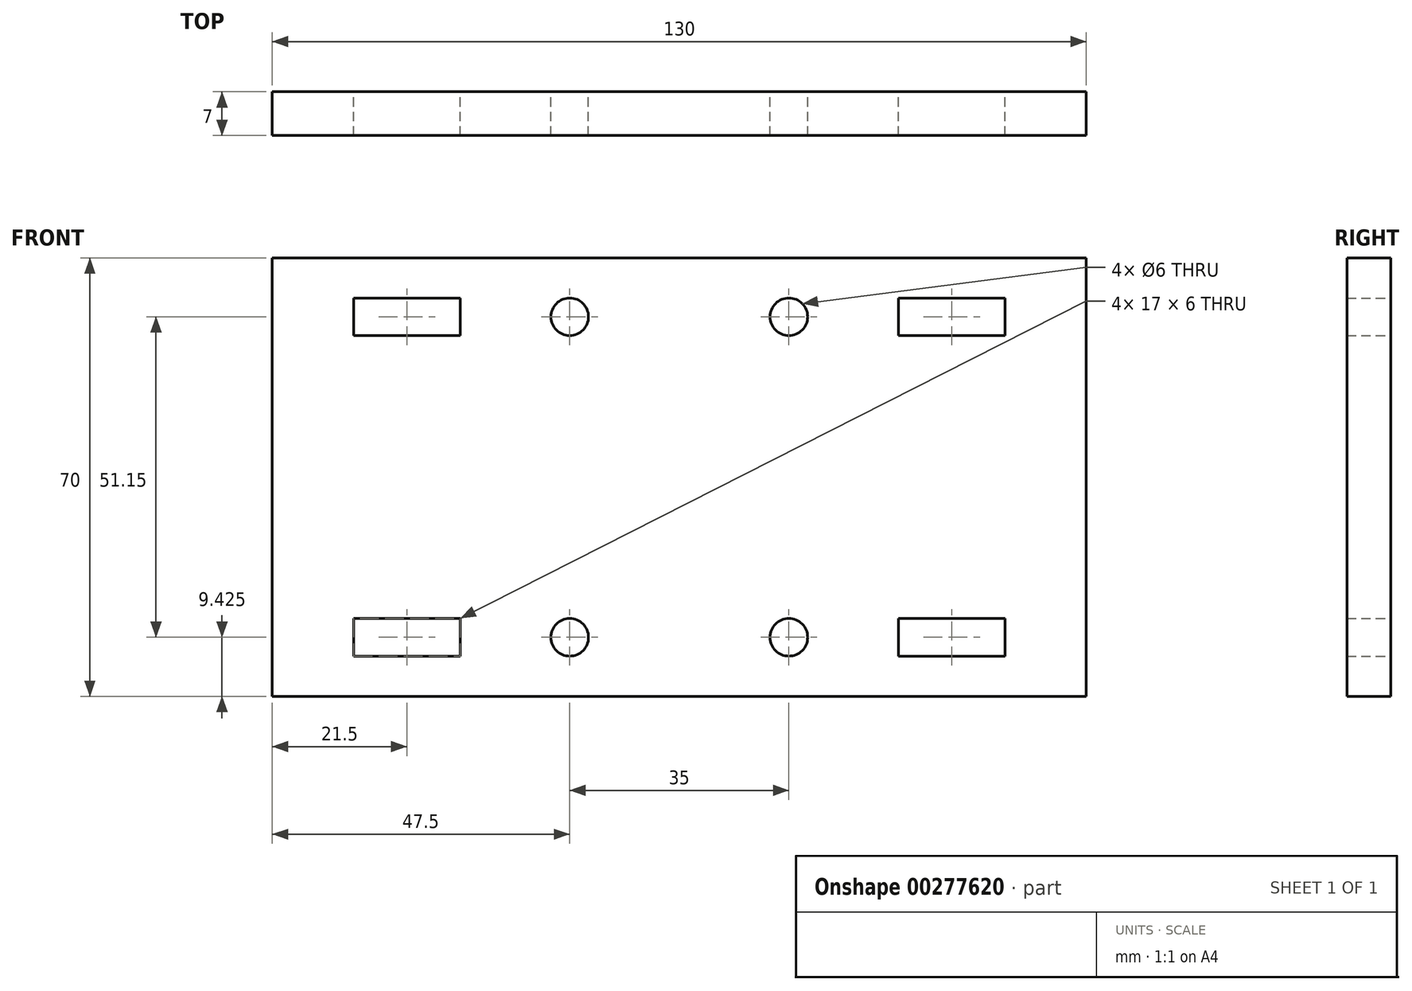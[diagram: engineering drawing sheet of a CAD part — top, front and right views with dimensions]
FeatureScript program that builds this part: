
annotation { "Feature Type Name" : "Feature", "Feature Type Description" : "" }
export const myFeature = defineFeature(function(context is Context, id is Id, definition is map)
    precondition{}
    {
        {
            var Q0;
            Q0=qCreatedBy(makeId("Front.planeOp"),FACE);
            var sketch = newSketch(context, id + "F0", { "sketchPlane" : qUnion([Q0])});
            skLineSegment(sketch, "E0.bottom", {"start": v(-65, 35) * mm, "end": v(65, 35) * mm});
            skLineSegment(sketch, "E0.top", {"start": v(-65, -35) * mm, "end": v(65, -35) * mm});
            skLineSegment(sketch, "E0.left", {"start": v(-65, 35) * mm, "end": v(-65, -35) * mm});
            skLineSegment(sketch, "E0.right", {"start": v(65, 35) * mm, "end": v(65, -35) * mm});
            skPoint(sketch, "E0.middle", {"position": v(0, 0) * mm});
            skLineSegment(sketch, "E1.bottom", {"start": v(-52, -28.58) * mm, "end": v(-35, -28.58) * mm});
            skLineSegment(sketch, "E1.top", {"start": v(-52, -22.58) * mm, "end": v(-35, -22.58) * mm});
            skLineSegment(sketch, "E1.left", {"start": v(-52, -28.58) * mm, "end": v(-52, -22.58) * mm});
            skLineSegment(sketch, "E1.right", {"start": v(-35, -28.58) * mm, "end": v(-35, -22.58) * mm});
            skCircle(sketch, "E2", {"center": v(-17.5, -25.58) * mm, "radius": 3 * mm});
            skCircle(sketch, "E3.MirrorC", {"center": v(17.5, -25.58) * mm, "radius": 3 * mm});
            skLineSegment(sketch, "E4.MirrorCS", {"start": v(52, -22.58) * mm, "end": v(35, -22.58) * mm});
            skLineSegment(sketch, "E5.MirrorCS", {"start": v(52, -28.58) * mm, "end": v(52, -22.58) * mm});
            skLineSegment(sketch, "E6.MirrorCS", {"start": v(52, -28.58) * mm, "end": v(35, -28.58) * mm});
            skLineSegment(sketch, "E7", {"start": v(35, -22.58) * mm, "end": v(35, -28.58) * mm});
            skLineSegment(sketch, "E8.MirrorCS", {"start": v(-52, 22.58) * mm, "end": v(-35, 22.58) * mm});
            skLineSegment(sketch, "E9.MirrorCS", {"start": v(-52, 28.58) * mm, "end": v(-52, 22.58) * mm});
            skLineSegment(sketch, "E10.MirrorCS", {"start": v(-52, 28.58) * mm, "end": v(-35, 28.58) * mm});
            skLineSegment(sketch, "E11.MirrorCS", {"start": v(-35, 28.58) * mm, "end": v(-35, 22.58) * mm});
            skCircle(sketch, "E12.MirrorC", {"center": v(-17.5, 25.58) * mm, "radius": 3 * mm});
            skCircle(sketch, "E13.MirrorC", {"center": v(17.5, 25.58) * mm, "radius": 3 * mm});
            skLineSegment(sketch, "E14.MirrorCS", {"start": v(35, 22.58) * mm, "end": v(35, 28.58) * mm});
            skLineSegment(sketch, "E15.MirrorCS", {"start": v(52, 22.58) * mm, "end": v(35, 22.58) * mm});
            skLineSegment(sketch, "E16.MirrorCS", {"start": v(52, 28.58) * mm, "end": v(52, 22.58) * mm});
            skLineSegment(sketch, "E17.MirrorCS", {"start": v(52, 28.58) * mm, "end": v(35, 28.58) * mm});
            skSolve(sketch);
        }
        {
            var Q0;
            Q0=makeQuery(id+"F0.imprint","IMPRINT",FACE,{"disambiguationData":[TD([[makeQuery(id+"F0.imprint","IMPRINT",EDGE,{"derivedFrom":sQuery(id+"F0.wireOp",EDGE,"E0.bottom")}),-1.0]])]});
            extrude(context, id + "F1", {"entities" : qUnion([Q0]), "depth" : 7 * mm});
        }
    });
